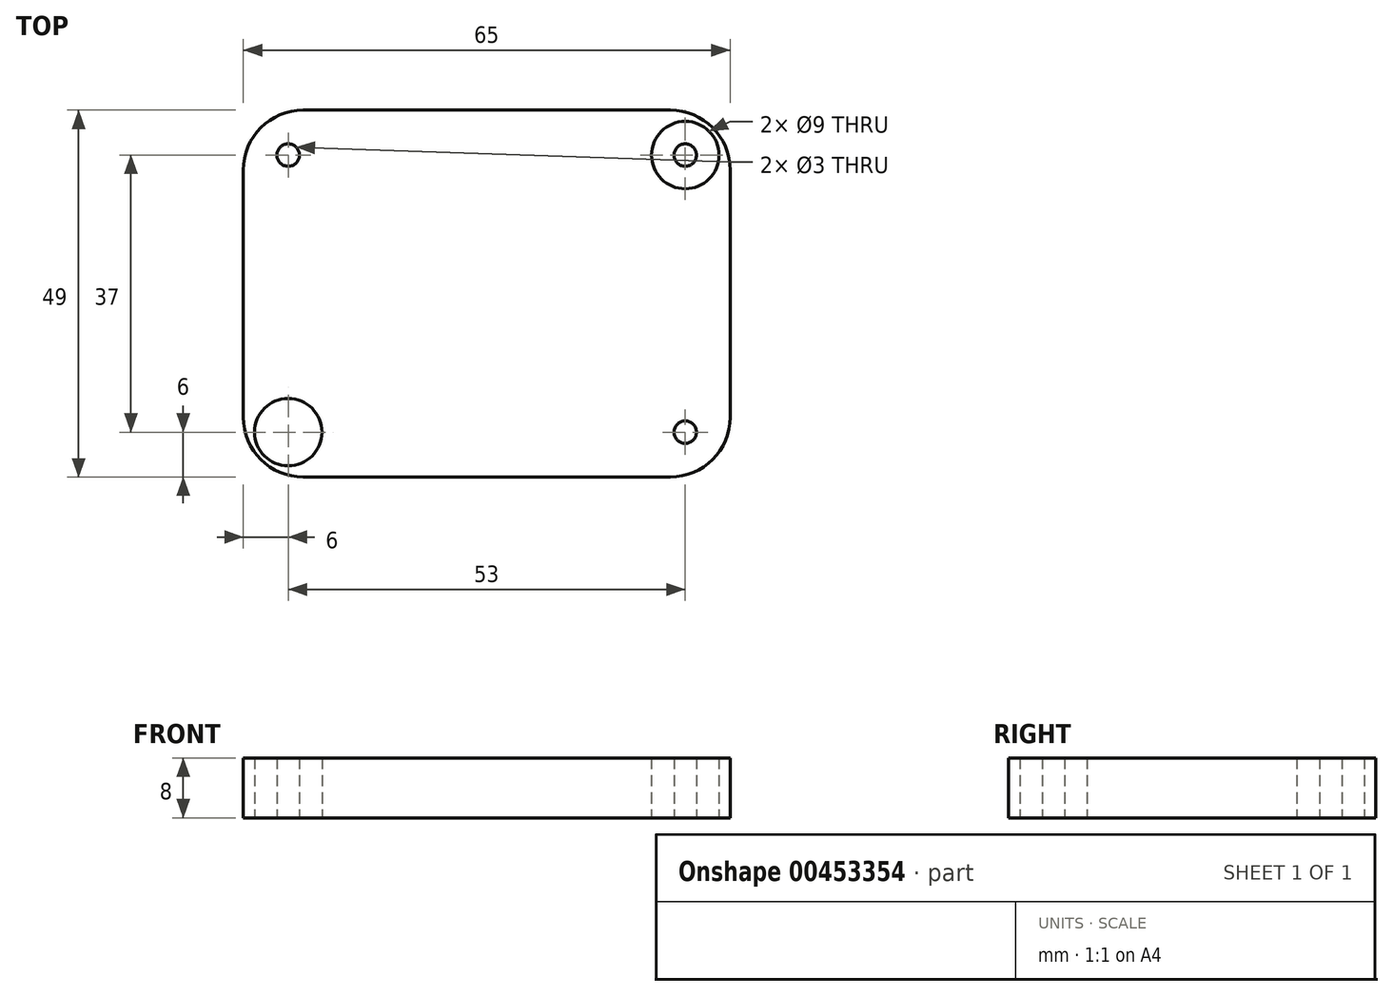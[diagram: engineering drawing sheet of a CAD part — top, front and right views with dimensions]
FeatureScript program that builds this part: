
annotation { "Feature Type Name" : "Feature", "Feature Type Description" : "" }
export const myFeature = defineFeature(function(context is Context, id is Id, definition is map)
    precondition{}
    {
        {
            var Q0;
            Q0=qCreatedBy(makeId("Top.planeOp"),FACE);
            var sketch = newSketch(context, id + "F0", { "sketchPlane" : qUnion([Q0])});
            skLineSegment(sketch, "E0.bottom", {"start": v(32.5, 24.5) * mm, "end": v(-32.5, 24.5) * mm});
            skLineSegment(sketch, "E0.top", {"start": v(32.5, -24.5) * mm, "end": v(-32.5, -24.5) * mm});
            skLineSegment(sketch, "E0.left", {"start": v(32.5, 24.5) * mm, "end": v(32.5, -24.5) * mm});
            skLineSegment(sketch, "E0.right", {"start": v(-32.5, 24.5) * mm, "end": v(-32.5, -24.5) * mm});
            skPoint(sketch, "E0.middle", {"position": v(0, 0) * mm});
            skLineSegment(sketch, "E1.bottom", {"start": v(26.5, 18.5) * mm, "end": v(-26.5, 18.5) * mm, "construction": true});
            skLineSegment(sketch, "E1.top", {"start": v(26.5, -18.5) * mm, "end": v(-26.5, -18.5) * mm, "construction": true});
            skLineSegment(sketch, "E1.left", {"start": v(26.5, 18.5) * mm, "end": v(26.5, -18.5) * mm, "construction": true});
            skLineSegment(sketch, "E1.right", {"start": v(-26.5, 18.5) * mm, "end": v(-26.5, -18.5) * mm, "construction": true});
            skLineSegment(sketch, "E2", {"start": v(0, 42.48) * mm, "end": v(0, -70.4) * mm, "construction": true});
            skPoint(sketch, "E2.endSnap0", {"position": v(0, 18.5) * mm});
            skLineSegment(sketch, "E3", {"start": v(-47.33, 0) * mm, "end": v(69.83, 0) * mm, "construction": true});
            skCircle(sketch, "E4", {"center": v(-26.5, 18.5) * mm, "radius": 1.5 * mm});
            skCircle(sketch, "E5.0", {"center": v(-26.5, 18.5) * mm, "radius": 4.5 * mm});
            skCircle(sketch, "E6.MirrorC", {"center": v(26.5, 18.5) * mm, "radius": 1.5 * mm});
            skCircle(sketch, "E7.MirrorC", {"center": v(26.5, 18.5) * mm, "radius": 4.5 * mm});
            skCircle(sketch, "E8.MirrorC", {"center": v(-26.5, -18.5) * mm, "radius": 4.5 * mm});
            skLineSegment(sketch, "E9.MirrorCS", {"start": v(-26.5, -18.5) * mm, "end": v(-26.5, 18.5) * mm, "construction": true});
            skCircle(sketch, "E10.MirrorC", {"center": v(-26.5, -18.5) * mm, "radius": 1.5 * mm});
            skCircle(sketch, "E11.MirrorC", {"center": v(26.5, -18.5) * mm, "radius": 4.5 * mm});
            skCircle(sketch, "E12.MirrorC", {"center": v(26.5, -18.5) * mm, "radius": 1.5 * mm});
            skSolve(sketch);
        }
        {
            var Q0;
            Q0 = qSketchRegion(id + "F0", true);
            extrude(context, id + "F1", {"entities" : qUnion([Q0]), "depth" : 1 * mm});
        }
        {
            var Q0;
            Q0=makeQuery(id+"F0.imprint","IMPRINT",FACE,{"disambiguationData":[TD([[makeQuery(id+"F0.imprint","IMPRINT",EDGE,{"derivedFrom":sQuery(id+"F0.wireOp",EDGE,"E0.bottom")}),1.0]])]});
            var sketch = newSketch(context, id + "F2", { "sketchPlane" : qUnion([Q0])});
            skSolve(sketch);
        }
        {
            var Q0;
            Q0 = qSketchRegion(id + "F2", true);
            var Q1;
            Q1=makeQuery(id+"F0.imprint","IMPRINT",FACE,{"disambiguationData":[TD([[makeQuery(id+"F0.imprint","IMPRINT",EDGE,{"derivedFrom":sQuery(id+"F0.wireOp",EDGE,"E6.MirrorC")}),1.0]])]});
            var Q2;
            Q2=makeQuery(id+"F0.imprint","IMPRINT",FACE,{"disambiguationData":[TD([[makeQuery(id+"F0.imprint","IMPRINT",EDGE,{"derivedFrom":sQuery(id+"F0.wireOp",EDGE,"E8.MirrorC")}),-1.0]])]});
            var Q3;
            Q3=makeQuery(id+"F0.imprint","IMPRINT",FACE,{"disambiguationData":[TD([[makeQuery(id+"F0.imprint","IMPRINT",EDGE,{"derivedFrom":sQuery(id+"F0.wireOp",EDGE,"E4")}),-1.0]])]});
            var Q4;
            Q4=makeQuery(id+"F0.imprint","IMPRINT",FACE,{"disambiguationData":[TD([[makeQuery(id+"F0.imprint","IMPRINT",EDGE,{"derivedFrom":sQuery(id+"F0.wireOp",EDGE,"E11.MirrorC")}),1.0]])]});
            extrude(context, id + "F3", {"entities" : qUnion([Q0, Q1, Q2, Q3, Q4]), "operationType" : NewBodyOperationType.ADD, "depth" : 8 * mm});
        }
        {
            var Q0;
            Q0=makeQuery(id+"F1.opExtrude","SWEPT_EDGE",EDGE,{"disambiguationData":[OSD([sQuery(id+"F0.wireOp",EDGE,"E0.top"),sQuery(id+"F0.wireOp",EDGE,"E0.left")])]});
            var Q1;
            Q1=makeQuery(id+"F1.opExtrude","SWEPT_EDGE",EDGE,{"disambiguationData":[OSD([sQuery(id+"F0.wireOp",EDGE,"E0.bottom"),sQuery(id+"F0.wireOp",EDGE,"E0.left")])]});
            var Q2;
            Q2=makeQuery(id+"F1.opExtrude","SWEPT_EDGE",EDGE,{"disambiguationData":[OSD([sQuery(id+"F0.wireOp",EDGE,"E0.top"),sQuery(id+"F0.wireOp",EDGE,"E0.right")])]});
            var Q3;
            Q3=makeQuery(id+"F1.opExtrude","SWEPT_EDGE",EDGE,{"disambiguationData":[OSD([sQuery(id+"F0.wireOp",EDGE,"E0.bottom"),sQuery(id+"F0.wireOp",EDGE,"E0.right")])]});
            fillet(context, id + "F4", {"entities" : qUnion([Q0, Q1, Q2, Q3]), "radius" : 8 * mm, "tangentPropagation" : true, "allowEdgeOverflow" : false});
        }
    });
